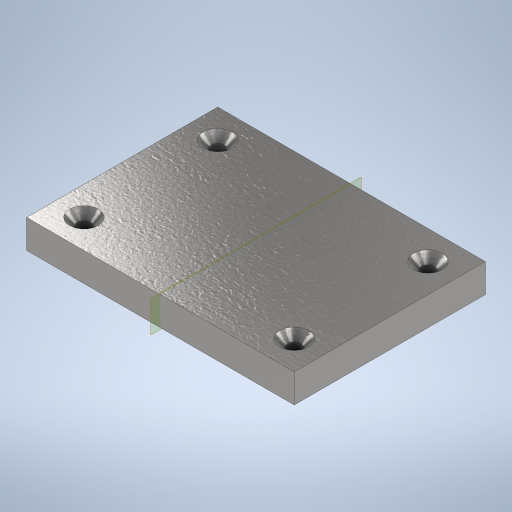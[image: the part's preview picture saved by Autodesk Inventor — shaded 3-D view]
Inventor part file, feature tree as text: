
AUTODESK INVENTOR PART (.ipt)
format: ipt  version: 2024 (Build 280153000, 153)  size: 320,000 bytes
history: native  units: mm
features: plane x2, sketch x2, extrude x1, hole x1, mirror x1
ambient origin geometry x8: Origin, YZ Plane, XZ Plane, XY Plane, X Axis, Y Axis, Z Axis, Center Point
bodies: Volumenkörper1 (feature_tree)
feature tree (7):
  extrude  "Extrusion1"  Depth=20.0mm
  hole  "Bohrung1"  [1 undecoded]
  plane  "Arbeitsebene1"
  mirror  "Spiegeln1"
  sketch  "Skizze1"  dims[d0=28.0mm d1=20.0mm]
  sketch  "Skizze2"  dims[d2=3.0mm d3=0.0mm d4=14.0mm d5=3.0mm d6=1.4mm d7=6.0mm d8=3.0mm d9=2.0mm d10=90.0deg d11=8.0mm d12=20.594885mm d13=14.0mm]
  plane  "Arbeitsebene2"
note: 1 required parameter value undecoded (feature->parameter linkage not recoverable at this tier; creation-order binding heuristic only, values carry confidence <= 0.55)
